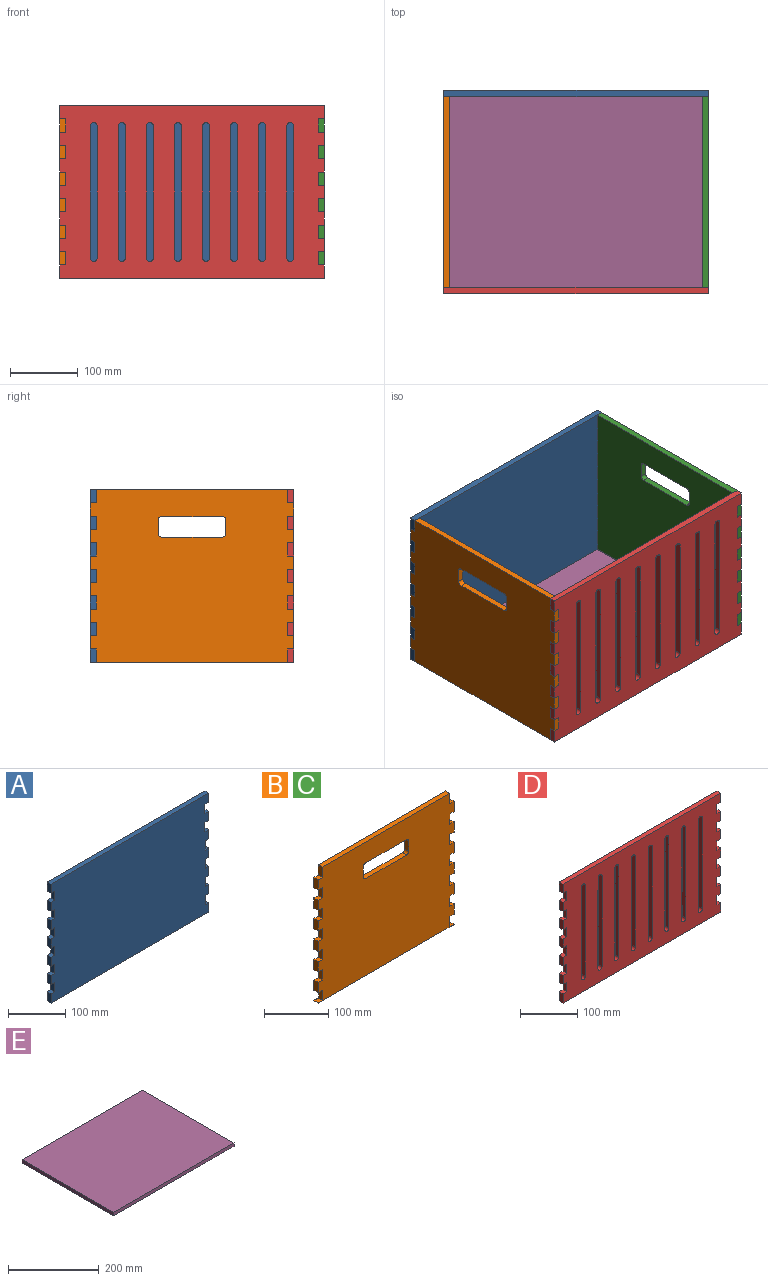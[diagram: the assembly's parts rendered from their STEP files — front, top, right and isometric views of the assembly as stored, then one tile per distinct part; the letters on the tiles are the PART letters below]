
ASSEMBLY  parts=5 mates=4
PART A: 59 faces, bbox 390x9x255 mm
  f0: plane 390x255mm, normal (0,1,0), area 93981mm2, adj f1,f2,f3,f4,f5,f6,f7,f8
  f1: plane 9x9mm, normal (0,0,-1), area 81mm2, adj f0,f2,f52,f53
  f2: plane 19.6x9mm, normal (1,0,0), area 176.4mm2, adj f0,f1,f3,f53
  f3: plane 390x9mm, normal (0,0,1), area 3510mm2, adj f0,f2,f4,f53
  f4: plane 19.6x9mm, normal (-1,0,0), area 176.4mm2, adj f0,f3,f5,f53
  f5: plane 9x9mm, normal (0,0,-1), area 81mm2, adj f0,f4,f6,f53
  f6: plane 19.6x9mm, normal (-1,0,0), area 176.4mm2, adj f0,f5,f7,f53
  f7: plane 9x9mm, normal (0,0,1), area 81mm2, adj f0,f6,f8,f53
  f8: plane 19.6x9mm, normal (-1,0,0), area 176.4mm2, adj f0,f7,f9,f53
  f9: plane 9x8.92mm, normal (0,0,-1), area 80.2mm2, adj f0,f8,f10,f53
  f10: plane 19.6x9mm, normal (-1,0,0), area 176.4mm2, adj f0,f9,f11,f53
  f11: plane 9x8.92mm, normal (0,0,1), area 80.2mm2, adj f0,f10,f12,f53
  f12: plane 19.6x9mm, normal (-1,0,0), area 176.4mm2, adj f0,f11,f13,f53
  f13: plane 9x8.83mm, normal (0,0,-1), area 79.5mm2, adj f0,f12,f14,f53
  f14: plane 19.6x9mm, normal (-1,0,0), area 176.4mm2, adj f0,f13,f15,f53
  f15: plane 9x8.83mm, normal (0,0,1), area 79.5mm2, adj f0,f14,f16,f53
  f16: plane 19.6x9mm, normal (-1,0,0), area 176.4mm2, adj f0,f15,f17,f53
  f17: plane 9x8.75mm, normal (0,0,-1), area 78.7mm2, adj f0,f16,f18,f53
  f18: plane 19.6x9mm, normal (-1,0,0), area 176.4mm2, adj f0,f17,f19,f53
  f19: plane 9x8.75mm, normal (0,0,1), area 78.7mm2, adj f0,f18,f20,f53
  f20: plane 19.6x9mm, normal (-1,0,0), area 176.4mm2, adj f0,f19,f21,f53
  f21: plane 9x8.66mm, normal (0,0,-1), area 78mm2, adj f0,f20,f22,f53
  f22: plane 19.6x9mm, normal (-1,0,0), area 176.4mm2, adj f0,f21,f23,f53
  f23: plane 9x8.66mm, normal (0,0,1), area 78mm2, adj f0,f22,f24,f53
  f24: plane 19.6x9mm, normal (-1,0,0), area 176.4mm2, adj f0,f23,f25,f53
  f25: plane 9x8.58mm, normal (0,0,-1), area 77.2mm2, adj f0,f24,f26,f53
  f26: plane 19.6x9mm, normal (-1,0,0), area 176.4mm2, adj f0,f25,f27,f53
  f27: plane 9x8.58mm, normal (0,0,1), area 77.2mm2, adj f0,f26,f28,f53
  f28: plane 19.8x9mm, normal (-1,0,0), area 178.2mm2, adj f0,f27,f29,f53
  f29: plane 390x9mm, normal (0,0,-1), area 3510mm2, adj f0,f28,f30,f53
  f30: plane 19.8x9mm, normal (1,0,0), area 178.2mm2, adj f0,f29,f31,f53
  f31: plane 9x8.58mm, normal (0,0,1), area 77.2mm2, adj f0,f30,f32,f53
  f32: plane 19.6x9mm, normal (1,0,0), area 176.4mm2, adj f0,f31,f33,f53
  f33: plane 9x8.58mm, normal (0,0,-1), area 77.2mm2, adj f0,f32,f34,f53
  f34: plane 19.6x9mm, normal (1,0,0), area 176.4mm2, adj f0,f33,f35,f53
  f35: plane 9x8.66mm, normal (0,0,1), area 78mm2, adj f0,f34,f36,f53
  f36: plane 19.6x9mm, normal (1,0,0), area 176.4mm2, adj f0,f35,f37,f53
  f37: plane 9x8.66mm, normal (0,0,-1), area 78mm2, adj f0,f36,f38,f53
  f38: plane 19.6x9mm, normal (1,0,0), area 176.4mm2, adj f0,f37,f39,f53
  f39: plane 9x8.75mm, normal (0,0,1), area 78.7mm2, adj f0,f38,f40,f53
  f40: plane 19.6x9mm, normal (1,0,0), area 176.4mm2, adj f0,f39,f41,f53
  f41: plane 9x8.75mm, normal (0,0,-1), area 78.7mm2, adj f0,f40,f42,f53
  f42: plane 19.6x9mm, normal (1,0,0), area 176.4mm2, adj f0,f41,f43,f53
  f43: plane 9x8.83mm, normal (0,0,1), area 79.5mm2, adj f0,f42,f44,f53
  f44: plane 19.6x9mm, normal (1,0,0), area 176.4mm2, adj f0,f43,f45,f53
  f45: plane 9x8.83mm, normal (0,0,-1), area 79.5mm2, adj f0,f44,f46,f53
  f46: plane 19.6x9mm, normal (1,0,0), area 176.4mm2, adj f0,f45,f47,f53
  f47: plane 9x8.92mm, normal (0,0,1), area 80.2mm2, adj f0,f46,f48,f53
  f48: plane 19.6x9mm, normal (1,0,0), area 176.4mm2, adj f0,f47,f49,f53
  f49: plane 9x8.92mm, normal (0,0,-1), area 80.2mm2, adj f0,f48,f50,f53
  f50: plane 19.6x9mm, normal (1,0,0), area 176.4mm2, adj f0,f49,f51,f53
  f51: plane 9x9mm, normal (0,0,1), area 81mm2, adj f0,f50,f52,f53
  f52: plane 19.6x9mm, normal (1,0,0), area 176.4mm2, adj f0,f1,f51,f53
  f53: plane 390x255mm, normal (0,-1,0), area 97383mm2, adj f1,f2,f3,f4,f5,f6,f7,f8
  f54: plane 378x2mm, normal (0,0,-1), area 756mm2, adj f0,f55,f57,f58
  f55: plane 9x2mm, normal (-1,0,0), area 18mm2, adj f0,f54,f56,f58
  f56: plane 378x2mm, normal (0,0,1), area 756mm2, adj f0,f55,f57,f58
  f57: plane 9x2mm, normal (1,0,0), area 18mm2, adj f0,f54,f56,f58
  f58: plane 378x9mm, normal (0,1,0), area 3402mm2, adj f54,f55,f56,f57
PART B: 70 faces, bbox 300x9x255 mm
  f0: plane 300x3mm, normal (0,1,0), area 849.6mm2, adj f1,f31,f32,f33,f34,f35,f36,f68
  f1: plane 19.6x9mm, normal (1,0,0), area 158.4mm2, adj f0,f36,f37,f65,f66,f67,f68,f69
  f2: cylinder r=5mm len=9mm, axis (0,1,0), area 70.7mm2, adj f3,f64,f65,f66
  f3: plane 90x9mm, normal (0,0,-1), area 810mm2, adj f2,f4,f65,f66
  f4: cylinder r=5mm len=9mm, axis (0,1,0), area 70.7mm2, adj f3,f5,f65,f66
  f5: plane 20x9mm, normal (-1,0,0), area 180mm2, adj f4,f6,f65,f66
  f6: cylinder r=5mm len=9mm, axis (0,1,0), area 70.7mm2, adj f5,f7,f65,f66
  f7: plane 90x9mm, normal (0,0,1), area 810mm2, adj f6,f8,f65,f66
  f8: cylinder r=5mm len=9mm, axis (0,1,0), area 70.7mm2, adj f7,f64,f65,f66
  f9: plane 19.6x9mm, normal (-1,0,0), area 176.4mm2, adj f10,f63,f65,f66
  f10: plane 9x9mm, normal (0,0,-1), area 81mm2, adj f9,f11,f65,f66
  f11: plane 19.6x9mm, normal (-1,0,0), area 176.4mm2, adj f10,f12,f65,f66
  f12: plane 9x9mm, normal (0,0,1), area 81mm2, adj f11,f13,f65,f66
  f13: plane 19.6x9mm, normal (-1,0,0), area 176.4mm2, adj f12,f14,f65,f66
  f14: plane 9x9mm, normal (0,0,-1), area 81mm2, adj f13,f15,f65,f66
  f15: plane 19.6x9mm, normal (-1,0,0), area 176.4mm2, adj f14,f16,f65,f66
  f16: plane 9x9mm, normal (0,0,1), area 81mm2, adj f15,f17,f65,f66
  f17: plane 19.6x9mm, normal (-1,0,0), area 176.4mm2, adj f16,f18,f65,f66
  f18: plane 9x9mm, normal (0,0,-1), area 81mm2, adj f17,f19,f65,f66
  f19: plane 19.6x9mm, normal (-1,0,0), area 176.4mm2, adj f18,f20,f65,f66
  f20: plane 9x9mm, normal (0,0,1), area 81mm2, adj f19,f21,f65,f66
  f21: plane 19.6x9mm, normal (-1,0,0), area 176.4mm2, adj f20,f22,f65,f66
  f22: plane 9x9mm, normal (0,0,-1), area 81mm2, adj f21,f23,f65,f66
  f23: plane 19.6x9mm, normal (-1,0,0), area 176.4mm2, adj f22,f24,f65,f66
  f24: plane 9x9mm, normal (0,0,1), area 81mm2, adj f23,f25,f65,f66
  f25: plane 19.6x9mm, normal (-1,0,0), area 176.4mm2, adj f24,f26,f65,f66
  f26: plane 9x9mm, normal (0,0,-1), area 81mm2, adj f25,f27,f65,f66
  f27: plane 19.6x9mm, normal (-1,0,0), area 176.4mm2, adj f26,f28,f65,f66
  f28: plane 9x9mm, normal (0,0,1), area 81mm2, adj f27,f29,f65,f66
  f29: plane 19.6x9mm, normal (-1,0,0), area 176.4mm2, adj f28,f30,f65,f66
  f30: plane 9x9mm, normal (0,0,-1), area 81mm2, adj f29,f31,f65,f66
  f31: plane 19.6x9mm, normal (-1,0,0), area 158.4mm2, adj f0,f30,f32,f65,f66,f67,f68,f69
  f32: plane 9x9mm, normal (0,0,1), area 81mm2, adj f0,f31,f33,f65
  f33: plane 9x0.2mm, normal (-1,0,0), area 1.8mm2, adj f0,f32,f34,f65
  f34: plane 300x9mm, normal (0,0,-1), area 2700mm2, adj f0,f33,f35,f65
  f35: plane 9x0.2mm, normal (1,0,0), area 1.8mm2, adj f0,f34,f36,f65
  f36: plane 9x9mm, normal (0,0,1), area 81mm2, adj f0,f1,f35,f65
  f37: plane 9x9mm, normal (0,0,-1), area 81mm2, adj f1,f38,f65,f66
  f38: plane 19.6x9mm, normal (1,0,0), area 176.4mm2, adj f37,f39,f65,f66
  f39: plane 9x9mm, normal (0,0,1), area 81mm2, adj f38,f40,f65,f66
  f40: plane 19.6x9mm, normal (1,0,0), area 176.4mm2, adj f39,f41,f65,f66
  f41: plane 9x9mm, normal (0,0,-1), area 81mm2, adj f40,f42,f65,f66
  f42: plane 19.6x9mm, normal (1,0,0), area 176.4mm2, adj f41,f43,f65,f66
  f43: plane 9x9mm, normal (0,0,1), area 81mm2, adj f42,f44,f65,f66
  f44: plane 19.6x9mm, normal (1,0,0), area 176.4mm2, adj f43,f45,f65,f66
  f45: plane 9x9mm, normal (0,0,-1), area 81mm2, adj f44,f46,f65,f66
  f46: plane 19.6x9mm, normal (1,0,0), area 176.4mm2, adj f45,f47,f65,f66
  f47: plane 9x9mm, normal (0,0,1), area 81mm2, adj f46,f48,f65,f66
  f48: plane 19.6x9mm, normal (1,0,0), area 176.4mm2, adj f47,f49,f65,f66
  f49: plane 9x9mm, normal (0,0,-1), area 81mm2, adj f48,f50,f65,f66
  f50: plane 19.6x9mm, normal (1,0,0), area 176.4mm2, adj f49,f51,f65,f66
  f51: plane 9x9mm, normal (0,0,1), area 81mm2, adj f50,f52,f65,f66
  f52: plane 19.6x9mm, normal (1,0,0), area 176.4mm2, adj f51,f53,f65,f66
  f53: plane 9x9mm, normal (0,0,-1), area 81mm2, adj f52,f54,f65,f66
  f54: plane 19.6x9mm, normal (1,0,0), area 176.4mm2, adj f53,f55,f65,f66
  f55: plane 9x9mm, normal (0,0,1), area 81mm2, adj f54,f56,f65,f66
  f56: plane 19.6x9mm, normal (1,0,0), area 176.4mm2, adj f55,f57,f65,f66
  f57: plane 9x9mm, normal (0,0,-1), area 81mm2, adj f56,f58,f65,f66
  f58: plane 19.6x9mm, normal (1,0,0), area 176.4mm2, adj f57,f59,f65,f66
  f59: plane 9x9mm, normal (0,0,1), area 81mm2, adj f58,f60,f65,f66
  f60: plane 19.6x9mm, normal (1,0,0), area 176.4mm2, adj f59,f61,f65,f66
  f61: plane 282x9mm, normal (0,0,1), area 2538mm2, adj f60,f62,f65,f66
  f62: plane 19.6x9mm, normal (-1,0,0), area 176.4mm2, adj f61,f63,f65,f66
  f63: plane 9x9mm, normal (0,0,1), area 81mm2, adj f9,f62,f65,f66
  f64: plane 20x9mm, normal (1,0,0), area 180mm2, adj f2,f8,f65,f66
  f65: plane 300x255mm, normal (0,-1,0), area 71051.9mm2, adj f1,f2,f3,f4,f5,f6,f7,f8
  f66: plane 300x243mm, normal (0,1,0), area 67664.3mm2, adj f1,f2,f3,f4,f5,f6,f7,f8
  f67: plane 282x2mm, normal (0,0,-1), area 564mm2, adj f1,f31,f66,f69
  f68: plane 282x2mm, normal (0,0,1), area 564mm2, adj f0,f1,f31,f69
  f69: plane 282x9mm, normal (0,1,0), area 2538mm2, adj f1,f31,f67,f68
PART C: same geometry as B
PART D: 91 faces, bbox 390x9x255 mm
  f0: cylinder r=5mm len=10mm, axis (0,1,0), area 141.4mm2, adj f1,f83,f84,f85
  f1: plane 195x9mm, normal (1,0,0), area 1755mm2, adj f0,f2,f84,f85
  f2: cylinder r=5mm len=10mm, axis (0,1,0), area 141.4mm2, adj f1,f83,f84,f85
  f3: cylinder r=5mm len=10mm, axis (0,1,0), area 141.4mm2, adj f4,f75,f84,f85
  f4: plane 195x9mm, normal (1,0,0), area 1755mm2, adj f3,f5,f84,f85
  f5: cylinder r=5mm len=10mm, axis (0,1,0), area 141.4mm2, adj f4,f75,f84,f85
  f6: cylinder r=5mm len=10mm, axis (0,1,0), area 141.4mm2, adj f7,f76,f84,f85
  f7: plane 195x9mm, normal (1,0,0), area 1755mm2, adj f6,f8,f84,f85
  f8: cylinder r=5mm len=10mm, axis (0,1,0), area 141.4mm2, adj f7,f76,f84,f85
  f9: cylinder r=5mm len=10mm, axis (0,1,0), area 141.4mm2, adj f10,f77,f84,f85
  f10: plane 195x9mm, normal (1,0,0), area 1755mm2, adj f9,f11,f84,f85
  f11: cylinder r=5mm len=10mm, axis (0,1,0), area 141.4mm2, adj f10,f77,f84,f85
  f12: cylinder r=5mm len=10mm, axis (0,1,0), area 141.4mm2, adj f13,f78,f84,f85
  f13: plane 195x9mm, normal (1,0,0), area 1755mm2, adj f12,f14,f84,f85
  f14: cylinder r=5mm len=10mm, axis (0,1,0), area 141.4mm2, adj f13,f78,f84,f85
  f15: cylinder r=5mm len=10mm, axis (0,1,0), area 141.4mm2, adj f16,f79,f84,f85
  f16: plane 195x9mm, normal (1,0,0), area 1755mm2, adj f15,f17,f84,f85
  f17: cylinder r=5mm len=10mm, axis (0,1,0), area 141.4mm2, adj f16,f79,f84,f85
  f18: cylinder r=5mm len=10mm, axis (0,1,0), area 141.4mm2, adj f19,f80,f84,f85
  f19: plane 195x9mm, normal (1,0,0), area 1755mm2, adj f18,f20,f84,f85
  f20: cylinder r=5mm len=10mm, axis (0,1,0), area 141.4mm2, adj f19,f80,f84,f85
  f21: cylinder r=5mm len=10mm, axis (0,1,0), area 141.4mm2, adj f22,f81,f84,f85
  f22: plane 195x9mm, normal (-1,0,0), area 1755mm2, adj f21,f23,f84,f85
  f23: cylinder r=5mm len=10mm, axis (0,1,0), area 141.4mm2, adj f22,f81,f84,f85
  f24: plane 9x9mm, normal (0,0,-1), area 81mm2, adj f25,f82,f84,f85
  f25: plane 19.6x9mm, normal (1,0,0), area 176.4mm2, adj f24,f26,f84,f85
  f26: plane 390x9mm, normal (0,0,1), area 3510mm2, adj f25,f27,f84,f85
  f27: plane 19.6x9mm, normal (-1,0,0), area 176.4mm2, adj f26,f28,f84,f85
  f28: plane 9x9mm, normal (0,0,-1), area 81mm2, adj f27,f29,f84,f85
  f29: plane 19.6x9mm, normal (-1,0,0), area 176.4mm2, adj f28,f30,f84,f85
  f30: plane 9x9mm, normal (0,0,1), area 81mm2, adj f29,f31,f84,f85
  f31: plane 19.6x9mm, normal (-1,0,0), area 176.4mm2, adj f30,f32,f84,f85
  f32: plane 9x9mm, normal (0,0,-1), area 81mm2, adj f31,f33,f84,f85
  f33: plane 19.6x9mm, normal (-1,0,0), area 176.4mm2, adj f32,f34,f84,f85
  f34: plane 9x9mm, normal (0,0,1), area 81mm2, adj f33,f35,f84,f85
  f35: plane 19.6x9mm, normal (-1,0,0), area 176.4mm2, adj f34,f36,f84,f85
  f36: plane 9x9mm, normal (0,0,-1), area 81mm2, adj f35,f37,f84,f85
  f37: plane 19.6x9mm, normal (-1,0,0), area 176.4mm2, adj f36,f38,f84,f85
  f38: plane 9x9mm, normal (0,0,1), area 81mm2, adj f37,f39,f84,f85
  f39: plane 19.6x9mm, normal (-1,0,0), area 176.4mm2, adj f38,f40,f84,f85
  f40: plane 9x9mm, normal (0,0,-1), area 81mm2, adj f39,f41,f84,f85
  f41: plane 19.6x9mm, normal (-1,0,0), area 176.4mm2, adj f40,f42,f84,f85
  f42: plane 9x9mm, normal (0,0,1), area 81mm2, adj f41,f43,f84,f85
  f43: plane 19.6x9mm, normal (-1,0,0), area 176.4mm2, adj f42,f44,f84,f85
  f44: plane 9x9mm, normal (0,0,-1), area 81mm2, adj f43,f45,f84,f85
  f45: plane 19.6x9mm, normal (-1,0,0), area 176.4mm2, adj f44,f46,f84,f85
  f46: plane 9x9mm, normal (0,0,1), area 81mm2, adj f45,f47,f84,f85
  f47: plane 19.6x9mm, normal (-1,0,0), area 176.4mm2, adj f46,f48,f84,f85
  f48: plane 9x9mm, normal (0,0,-1), area 81mm2, adj f47,f49,f84,f85
  f49: plane 19.6x9mm, normal (-1,0,0), area 176.4mm2, adj f48,f50,f84,f85
  f50: plane 9x9mm, normal (0,0,1), area 81mm2, adj f49,f51,f84,f85
  f51: plane 19.8x9mm, normal (-1,0,0), area 178.2mm2, adj f50,f52,f84,f85
  f52: plane 390x9mm, normal (0,0,-1), area 3510mm2, adj f51,f53,f84,f85
  f53: plane 19.8x9mm, normal (1,0,0), area 178.2mm2, adj f52,f54,f84,f85
  f54: plane 9x9mm, normal (0,0,1), area 81mm2, adj f53,f55,f84,f85
  f55: plane 19.6x9mm, normal (1,0,0), area 176.4mm2, adj f54,f56,f84,f85
  f56: plane 9x9mm, normal (0,0,-1), area 81mm2, adj f55,f57,f84,f85
  f57: plane 19.6x9mm, normal (1,0,0), area 176.4mm2, adj f56,f58,f84,f85
  f58: plane 9x9mm, normal (0,0,1), area 81mm2, adj f57,f59,f84,f85
  f59: plane 19.6x9mm, normal (1,0,0), area 176.4mm2, adj f58,f60,f84,f85
  f60: plane 9x9mm, normal (0,0,-1), area 81mm2, adj f59,f61,f84,f85
  f61: plane 19.6x9mm, normal (1,0,0), area 176.4mm2, adj f60,f62,f84,f85
  f62: plane 9x9mm, normal (0,0,1), area 81mm2, adj f61,f63,f84,f85
  f63: plane 19.6x9mm, normal (1,0,0), area 176.4mm2, adj f62,f64,f84,f85
  f64: plane 9x9mm, normal (0,0,-1), area 81mm2, adj f63,f65,f84,f85
  f65: plane 19.6x9mm, normal (1,0,0), area 176.4mm2, adj f64,f66,f84,f85
  f66: plane 9x9mm, normal (0,0,1), area 81mm2, adj f65,f67,f84,f85
  f67: plane 19.6x9mm, normal (1,0,0), area 176.4mm2, adj f66,f68,f84,f85
  f68: plane 9x9mm, normal (0,0,-1), area 81mm2, adj f67,f69,f84,f85
  f69: plane 19.6x9mm, normal (1,0,0), area 176.4mm2, adj f68,f70,f84,f85
  f70: plane 9x9mm, normal (0,0,1), area 81mm2, adj f69,f71,f84,f85
  f71: plane 19.6x9mm, normal (1,0,0), area 176.4mm2, adj f70,f72,f84,f85
  f72: plane 9x9mm, normal (0,0,-1), area 81mm2, adj f71,f73,f84,f85
  f73: plane 19.6x9mm, normal (1,0,0), area 176.4mm2, adj f72,f74,f84,f85
  f74: plane 9x9mm, normal (0,0,1), area 81mm2, adj f73,f82,f84,f85
  f75: plane 195x9mm, normal (-1,0,0), area 1755mm2, adj f3,f5,f84,f85
  f76: plane 195x9mm, normal (-1,0,0), area 1755mm2, adj f6,f8,f84,f85
  f77: plane 195x9mm, normal (-1,0,0), area 1755mm2, adj f9,f11,f84,f85
  f78: plane 195x9mm, normal (-1,0,0), area 1755mm2, adj f12,f14,f84,f85
  f79: plane 195x9mm, normal (-1,0,0), area 1755mm2, adj f15,f17,f84,f85
  f80: plane 195x9mm, normal (-1,0,0), area 1755mm2, adj f18,f20,f84,f85
  f81: plane 195x9mm, normal (1,0,0), area 1755mm2, adj f21,f23,f84,f85
  f82: plane 19.6x9mm, normal (1,0,0), area 176.4mm2, adj f24,f74,f84,f85
  f83: plane 195x9mm, normal (-1,0,0), area 1755mm2, adj f0,f2,f84,f85
  f84: plane 390x255mm, normal (0,-1,0), area 81104.9mm2, adj f0,f1,f2,f3,f4,f5,f6,f7
  f85: plane 390x255mm, normal (0,1,0), area 77702.9mm2, adj f0,f1,f2,f3,f4,f5,f6,f7
  f86: plane 9x2mm, normal (-1,0,0), area 18mm2, adj f85,f87,f89,f90
  f87: plane 378x2mm, normal (0,0,-1), area 756mm2, adj f85,f86,f88,f90
  f88: plane 9x2mm, normal (1,0,0), area 18mm2, adj f85,f87,f89,f90
  f89: plane 378x2mm, normal (0,0,1), area 756mm2, adj f85,f86,f88,f90
  f90: plane 378x9mm, normal (0,1,0), area 3402mm2, adj f86,f87,f88,f89
PART E: 6 faces, bbox 375x285x9 mm
  f0: plane 285x9mm, normal (-1,0,0), area 2565mm2, adj f1,f3,f4,f5
  f1: plane 375x9mm, normal (0,-1,0), area 3375mm2, adj f0,f2,f4,f5
  f2: plane 285x9mm, normal (1,0,0), area 2565mm2, adj f1,f3,f4,f5
  f3: plane 375x9mm, normal (0,1,0), area 3375mm2, adj f0,f2,f4,f5
  f4: plane 375x285mm, normal (0,0,1), area 106875mm2, adj f0,f1,f2,f3
  f5: plane 375x285mm, normal (0,0,-1), area 106875mm2, adj f0,f1,f2,f3
PLACE A rot(axis=(0,0,1),180deg) t=(75.23,210.86,73.97)mm
PLACE B rot(axis=(0,0,-1),90deg) t=(-110.77,69.86,73.97)mm
PLACE C rot(axis=(0,0,1),90deg) t=(261.23,69.86,73.97)mm
PLACE D t=(75.23,-71.14,73.97)mm
PLACE E t=(73.14,83.78,-50.53)mm
MATE fastened D.f85 <-> E.f1  axis (0,1,0) through (75.23,-71.14,-46.03)mm
MATE fastened C.f60 <-> A.f0  axis (0,1,0) through (270.23,210.86,191.67)mm
MATE fastened B.f62 <-> A.f0  axis (0,1,0) through (-115.27,210.86,191.67)mm
MATE fastened B.f60 <-> D.f85  axis (0,-1,0) through (-115.27,-71.14,191.67)mm
